# Revit family: Hager-Vector-IP55-sistema-CH-it
name_source: partatom
category: Electrical Equipment
units: mm (PartAtom-declared; Revit-internal decimal feet)

## family parameters
Cut with Voids When Loaded = No
Host = Face
Panel Configuration = Two Columns, Circuits Across
Part Type = Panelboard
Room Calculation Point = No
Round Connector Dimension = Use Diameter
Shared = No

## types (10) — shared parameters
EF000003 - Tipo di montaggio = EV000384 - A parete
EF000007 - colore = EV000270 - grigio
EF000116 - numero RAL = 7035
EF000118 - con piastra di montaggio = No
EF000339 - tipo di copertura = EV004216 - porta
EF001062 - esecuzione EMC = No
EF001088 - possibilità di applicazione = Yes
EF001134 - barra DIN = Yes
EF001596 - Attacco Lampada = EV000139 - plastica
EF004462 - tipo di chiusura = EV000154 - altri
EF005474 - grado di protezione (IP) = EV006421 - IP65
EF006244 - coperchio/porta trasparente = Yes
EF006306 - con serratura = No
EF009212 - esecuzione coperchio = EV000116 - chiuso
EF015776 - Morsettiera di terra = No
EF015777 - Morsettiera neutra = No
EF015941 - Segnale di passaggio porta = Yes
HG000001 - Numero di colonne = 1
HG000002 - Con porta = Yes
HG000003 - Gamma = Vector
HG000005 - Spessore = 3 mm  [stored 0.00984252 ft]
HG000006 - Ad incasso = No
HG000009 - Porta doppia a battente = No
HG000010 - Porte asimmetriche = No
HG000011 - File vuote nella parte basse = No
HG000017 - Distanza tra i poli = 18 mm  [stored 0.0590551 ft]
Manufacturer = Hager
Type Comments = Vector
zero-valued in all types: Default Elevation, EF000218 - profondità di incasso, EF000332 - Altezza della parte incassata, EF000846 - larghezza di montaggio, HG000007 - Numero di colonne vuote, HG000008 - Numero di file vuote

## per-type parameters (varying)
| type | EF000008 - Larghezza | EF000040 - Altezza | EF000049 - profondità | EF000266 - numero di file | EF001131 - profondità interna | EF002950 - Numero moduli DIN | HG000004 - Codice produttore | Model |
| A parete IP65 L111 A175 P93 3 Unità di divisione - VE103A | 111 mm | 175 mm | 93 mm | 1 | 93 mm | 3 | VE103A | VE103A |
| A parete IP65 L165 A190 P113 6 Unità di divisione - VE106A | 165 mm | 190 mm | 113 mm | 1 | 113 mm | 6 | VE106A | VE106A |
| A parete IP65 L237 A210 P114 10 Unità di divisione - VE110A | 237 mm | 210 mm | 114 mm | 1 | 114 mm | 10 | VE110A | VE110A |
| A parete IP65 L310 A302 P151 12 Unità di divisione - VE112AK | 310 mm | 302 mm | 151 mm  [stored 0.495407 ft] | 1 | 151 mm  [stored 0.495407 ft] | 12 | VE112AK | VE112AK |
| A parete IP65 L310 A427 P151 12 Unità di divisione - VE212AK | 310 mm | 427 mm | 151 mm  [stored 0.495407 ft] | 2 | 151 mm  [stored 0.495407 ft] | 12 | VE212AK | VE212AK |
| A parete IP65 L310 A552 P151 12 Unità di divisione - VE312AK | 310 mm | 552 mm | 151 mm  [stored 0.495407 ft] | 3 | 151 mm  [stored 0.495407 ft] | 12 | VE312AK | VE312AK |
| A parete IP65 L310 A677 P151 12 Unità di divisione - VE412AK | 310 mm | 677 mm | 151 mm  [stored 0.495407 ft] | 4 | 151 mm  [stored 0.495407 ft] | 12 | VE412AK | VE412AK |
| A parete IP65 L418 A302 P151 18 Unità di divisione - VE118AK | 418 mm  [stored 1.37139 ft] | 302 mm | 151 mm  [stored 0.495407 ft] | 1 | 151 mm  [stored 0.495407 ft] | 18 | VE118AK | VE118AK |
| A parete IP65 L418 A452 P151 18 Unità di divisione - VE218AK | 418 mm  [stored 1.37139 ft] | 452 mm | 151 mm  [stored 0.495407 ft] | 2 | 151 mm  [stored 0.495407 ft] | 18 | VE218AK | VE218AK |
| A parete IP65 L418 A602 P151 18 Unità di divisione - VE318AK | 418 mm  [stored 1.37139 ft] | 602 mm  [stored 1.97507 ft] | 151 mm  [stored 0.495407 ft] | 3 | 151 mm  [stored 0.495407 ft] | 18 | VE318AK | VE318AK |

note: [stored X ft] marks values corroborated as IEEE doubles in the binary element streams (Revit-internal decimal feet)

## geometry (parser evidence)
native form markers: Sweep x17
no freeform markers — native parametric forms only
